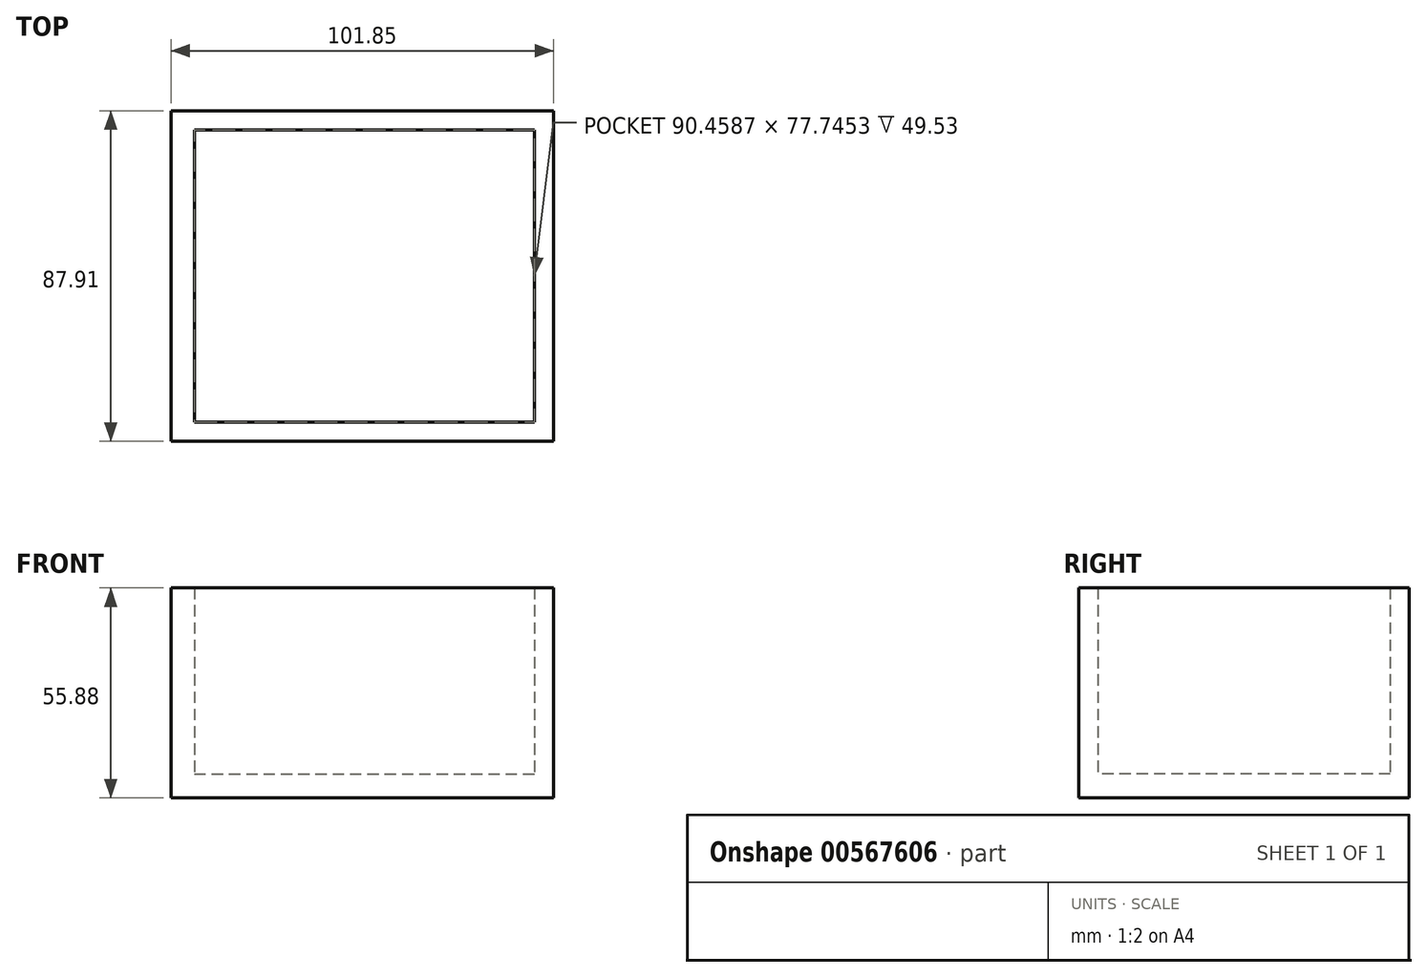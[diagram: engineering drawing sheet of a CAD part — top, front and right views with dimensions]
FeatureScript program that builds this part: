
annotation { "Feature Type Name" : "Feature", "Feature Type Description" : "" }
export const myFeature = defineFeature(function(context is Context, id is Id, definition is map)
    precondition{}
    {
        {
            var Q0;
            Q0=qCreatedBy(makeId("Top.planeOp"),FACE);
            var sketch = newSketch(context, id + "F0", { "sketchPlane" : qUnion([Q0])});
            skLineSegment(sketch, "E0.bottom", {"start": v(-62.2, 36.6) * mm, "end": v(28.26, 36.6) * mm});
            skLineSegment(sketch, "E0.top", {"start": v(-62.2, -41.15) * mm, "end": v(28.26, -41.15) * mm});
            skLineSegment(sketch, "E0.left", {"start": v(-62.2, 36.6) * mm, "end": v(-62.2, -41.15) * mm});
            skLineSegment(sketch, "E0.right", {"start": v(28.26, 36.6) * mm, "end": v(28.26, -41.15) * mm});
            skLineSegment(sketch, "E1.bottom", {"start": v(28.26, 36.6) * mm, "end": v(33.38, 36.6) * mm});
            skLineSegment(sketch, "E1.top", {"start": v(28.26, -41.15) * mm, "end": v(33.38, -41.15) * mm});
            skLineSegment(sketch, "E1.right", {"start": v(33.38, 36.6) * mm, "end": v(33.38, -41.15) * mm});
            skLineSegment(sketch, "E2.bottom", {"start": v(-62.2, 36.6) * mm, "end": v(33.38, 36.6) * mm});
            skLineSegment(sketch, "E2.top", {"start": v(-62.2, 41.64) * mm, "end": v(33.38, 41.64) * mm});
            skLineSegment(sketch, "E2.left", {"start": v(-62.2, 36.6) * mm, "end": v(-62.2, 41.64) * mm});
            skLineSegment(sketch, "E2.right", {"start": v(33.38, 36.6) * mm, "end": v(33.38, 41.64) * mm});
            skLineSegment(sketch, "E3.bottom", {"start": v(-62.2, -41.15) * mm, "end": v(33.38, -41.15) * mm});
            skLineSegment(sketch, "E3.top", {"start": v(-62.2, -46.27) * mm, "end": v(33.38, -46.27) * mm});
            skLineSegment(sketch, "E3.left", {"start": v(-62.2, -41.15) * mm, "end": v(-62.2, -46.27) * mm});
            skLineSegment(sketch, "E3.right", {"start": v(33.38, -41.15) * mm, "end": v(33.38, -46.27) * mm});
            skLineSegment(sketch, "E4.bottom", {"start": v(-62.2, 41.64) * mm, "end": v(-68.47, 41.64) * mm});
            skLineSegment(sketch, "E4.top", {"start": v(-62.2, -46.27) * mm, "end": v(-68.47, -46.27) * mm});
            skLineSegment(sketch, "E4.left", {"start": v(-62.2, 41.64) * mm, "end": v(-62.2, -46.27) * mm});
            skLineSegment(sketch, "E4.right", {"start": v(-68.47, 41.64) * mm, "end": v(-68.47, -46.27) * mm});
            skSolve(sketch);
        }
        {
            var Q0;
            {var subQ0=sQuery(id+"F0.wireOp",EDGE,"E0.right");Q0=makeQuery(id+"F0.imprint","IMPRINT",FACE,{"disambiguationData":[TD([[makeQuery(id+"F0.imprint","IMPRINT",EDGE,{"derivedFrom":subQ0}),-1.0]])]});}
            extrude(context, id + "F1", {"entities" : qUnion([Q0]), "depth" : 6.35 * mm, "offsetDistance" : 25.4 * mm});
        }
        {
            var Q0;
            Q0 = qSketchRegion(id + "F0", true);
            extrude(context, id + "F2", {"entities" : qUnion([Q0]), "operationType" : NewBodyOperationType.ADD, "depth" : 55.88 * mm, "offsetDistance" : 25.4 * mm});
        }
    });
